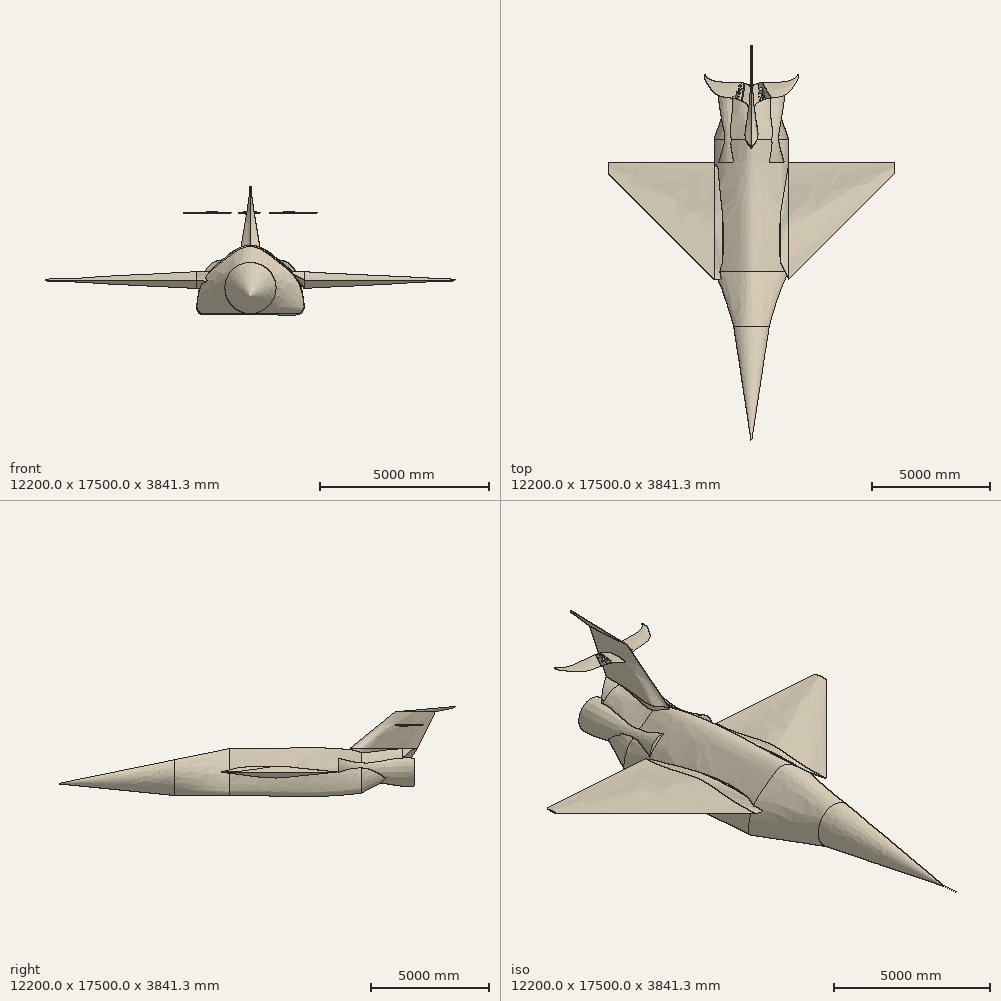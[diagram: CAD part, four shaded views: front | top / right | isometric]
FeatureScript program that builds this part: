
annotation { "Feature Type Name" : "Feature", "Feature Type Description" : "" }
export const myFeature = defineFeature(function(context is Context, id is Id, definition is map)
    precondition{}
    {
        {
            var Q0;
            Q0=qCreatedBy(makeId("Right.planeOp"),FACE);
            var sketch = newSketch(context, id + "F0", { "sketchPlane" : qUnion([Q0])});
            skLineSegment(sketch, "E0", {"start": v(0, 0) * mm, "end": v(-1750, 0) * mm});
            skLineSegment(sketch, "E1", {"start": v(-1750, 0) * mm, "end": v(-3500, 0) * mm});
            skLineSegment(sketch, "E2", {"start": v(-3500, 0) * mm, "end": v(-3500, -1000) * mm});
            skLineSegment(sketch, "E3", {"start": v(-3500, -1000) * mm, "end": v(-8500, -1000) * mm});
            skLineSegment(sketch, "E4", {"start": v(-8500, -1000) * mm, "end": v(-8500, -499.31) * mm});
            skLineSegment(sketch, "E5", {"start": v(-1151.4, 0) * mm, "end": v(-1151.4, 1000) * mm});
            skLineSegment(sketch, "E6", {"start": v(-1151.4, 1000) * mm, "end": v(-8500, -499.31) * mm});
            skLineSegment(sketch, "E7", {"start": v(-8500, -499.31) * mm, "end": v(-3500, -1000) * mm});
            skLineSegment(sketch, "E8", {"start": v(-3500, 0) * mm, "end": v(-3500, 520.82) * mm});
            skLineSegment(sketch, "E9", {"start": v(-8500, -499.31) * mm, "end": v(-8450, -499.31) * mm});
            skLineSegment(sketch, "E10", {"start": v(-8450, -499.31) * mm, "end": v(-8450, -489.1) * mm});
            skLineSegment(sketch, "E11", {"start": v(-8450, -499.31) * mm, "end": v(-8450, -504.32) * mm});
            skSolve(sketch);
        }
        {
            var Q0;
            Q0=sQuery(id+"F0.wireOp",EDGE,"E5");
            cPlane(context, id + "F1", {"entities" : qUnion([Q0]), "cplaneType" : CPlaneType.LINE_ANGLE, "offset" : 25 * mm, "angle" : 90 * degree, "oppositeDirection" : true, "width" : 150 * mm, "height" : 150 * mm});
        }
        {
            var Q0;
            Q0=qCreatedBy(id+"F1.planeOp",FACE);
            var sketch = newSketch(context, id + "F2", { "sketchPlane" : qUnion([Q0])});
            skLineSegment(sketch, "E12.top", {"start": v(-1394.2, -1000) * mm, "end": v(1394.2, -1000) * mm});
            skPoint(sketch, "E12.middle", {"position": v(0, 0) * mm});
            skFitSpline(sketch, "E13", {"points": [v(-1600, -1000) * mm, v(-848, 530) * mm, v(0, 1000) * mm, v(848, 530) * mm, v(1600, -1000) * mm], "startDerivative": vector(0, 10524.75) * mm, "endDerivative": vector(0, -10524.75) * mm});
            skArc(sketch, "E14", {"start": v(-735.27, 618.52) * mm, "mid": v(-1273.27, 435.52) * mm, "end": v(-1440.68, -107.53) * mm});
            skArc(sketch, "E15", {"start": v(1440.68, -107.53) * mm, "mid": v(1273.27, 435.52) * mm, "end": v(735.27, 618.52) * mm});
            skFitSpline(sketch, "E16.trimOffspring", {"points": [v(-1600, -1000) * mm, v(-848, 530) * mm, v(0, 1000) * mm, v(848, 530) * mm, v(1600, -1000) * mm], "startDerivative": vector(0, 10524.75) * mm, "endDerivative": vector(0, -10524.75) * mm});
            skFitSpline(sketch, "E17.trimOffspring", {"points": [v(-1600, -1000) * mm, v(-848, 530) * mm, v(0, 1000) * mm, v(848, 530) * mm, v(1600, -1000) * mm], "startDerivative": vector(0, 10524.75) * mm, "endDerivative": vector(0, -10524.75) * mm});
            skArc(sketch, "E18.filletArc", {"start": v(-1593.82, -787.83) * mm, "mid": v(-1539.85, -937.05) * mm, "end": v(-1394.2, -1000) * mm});
            skArc(sketch, "E19.filletArc", {"start": v(1394.2, -1000) * mm, "mid": v(1539.85, -937.05) * mm, "end": v(1593.82, -787.83) * mm});
            skSolve(sketch);
        }
        {
            var Q0;
            Q0=qCreatedBy(makeId("Front.planeOp"),FACE);
            var sketch = newSketch(context, id + "F3", { "sketchPlane" : qUnion([Q0])});
            skLineSegment(sketch, "E20.top", {"start": v(-1394.2, -1000) * mm, "end": v(1394.2, -1000) * mm});
            skPoint(sketch, "E20.middle", {"position": v(0, 0) * mm});
            skFitSpline(sketch, "E21", {"points": [v(-1600, -1000) * mm, v(-848, 530) * mm, v(0, 1000) * mm, v(848, 530) * mm, v(1600, -1000) * mm], "startDerivative": vector(0, 10524.75) * mm, "endDerivative": vector(0, -10524.75) * mm});
            skArc(sketch, "E22", {"start": v(-735.27, 618.52) * mm, "mid": v(-1273.27, 435.52) * mm, "end": v(-1440.68, -107.53) * mm});
            skArc(sketch, "E23", {"start": v(1440.68, -107.53) * mm, "mid": v(1273.27, 435.52) * mm, "end": v(735.27, 618.52) * mm});
            skFitSpline(sketch, "E24.trimOffspring", {"points": [v(-1600, -1000) * mm, v(-848, 530) * mm, v(0, 1000) * mm, v(848, 530) * mm, v(1600, -1000) * mm], "startDerivative": vector(0, 10524.75) * mm, "endDerivative": vector(0, -10524.75) * mm});
            skFitSpline(sketch, "E25.trimOffspring", {"points": [v(-1600, -1000) * mm, v(-848, 530) * mm, v(0, 1000) * mm, v(848, 530) * mm, v(1600, -1000) * mm], "startDerivative": vector(0, 10524.75) * mm, "endDerivative": vector(0, -10524.75) * mm});
            skArc(sketch, "E26.filletArc", {"start": v(-1593.82, -787.83) * mm, "mid": v(-1539.85, -937.05) * mm, "end": v(-1394.2, -1000) * mm});
            skArc(sketch, "E27.filletArc", {"start": v(1394.2, -1000) * mm, "mid": v(1539.85, -937.05) * mm, "end": v(1593.82, -787.83) * mm});
            skSolve(sketch);
        }
        {
            var Q0;
            Q0=qCreatedBy(makeId("Front.planeOp"),FACE);
            cPlane(context, id + "F4", {"entities" : qUnion([Q0]), "cplaneType" : CPlaneType.OFFSET, "offset" : 3500 * mm, "oppositeDirection" : true, "width" : 150 * mm, "height" : 150 * mm});
        }
        {
            var Q0;
            Q0=qCreatedBy(id+"F4.planeOp",FACE);
            var sketch = newSketch(context, id + "F5", { "sketchPlane" : qUnion([Q0])});
            skLineSegment(sketch, "E28.top", {"start": v(-1394.2, -1000) * mm, "end": v(1394.2, -1000) * mm});
            skPoint(sketch, "E28.middle", {"position": v(0, 0) * mm});
            skFitSpline(sketch, "E29", {"points": [v(-1600, -1000) * mm, v(-848, 530) * mm, v(0, 1000) * mm, v(848, 530) * mm, v(1600, -1000) * mm], "startDerivative": vector(0, 10524.75) * mm, "endDerivative": vector(0, -10524.75) * mm});
            skArc(sketch, "E30", {"start": v(-735.27, 618.52) * mm, "mid": v(-1273.27, 435.52) * mm, "end": v(-1440.68, -107.53) * mm});
            skArc(sketch, "E31", {"start": v(1440.68, -107.53) * mm, "mid": v(1273.27, 435.52) * mm, "end": v(735.27, 618.52) * mm});
            skFitSpline(sketch, "E32.trimOffspring", {"points": [v(-1600, -1000) * mm, v(-848, 530) * mm, v(0, 1000) * mm, v(848, 530) * mm, v(1600, -1000) * mm], "startDerivative": vector(0, 10524.75) * mm, "endDerivative": vector(0, -10524.75) * mm});
            skFitSpline(sketch, "E33.trimOffspring", {"points": [v(-1600, -1000) * mm, v(-848, 530) * mm, v(0, 1000) * mm, v(848, 530) * mm, v(1600, -1000) * mm], "startDerivative": vector(0, 10524.75) * mm, "endDerivative": vector(0, -10524.75) * mm});
            skArc(sketch, "E34.filletArc", {"start": v(-1593.82, -787.83) * mm, "mid": v(-1539.85, -937.05) * mm, "end": v(-1394.2, -1000) * mm});
            skArc(sketch, "E35.filletArc", {"start": v(1394.2, -1000) * mm, "mid": v(1539.85, -937.05) * mm, "end": v(1593.82, -787.83) * mm});
            skSolve(sketch);
        }
        {
            var Q0;
            Q0=qCreatedBy(makeId("Front.planeOp"),FACE);
            cPlane(context, id + "F6", {"entities" : qUnion([Q0]), "cplaneType" : CPlaneType.OFFSET, "offset" : 4500 * mm, "oppositeDirection" : true, "width" : 150 * mm, "height" : 150 * mm});
        }
        {
            var Q0;
            Q0=qCreatedBy(id+"F6.planeOp",FACE);
            var sketch = newSketch(context, id + "F7", { "sketchPlane" : qUnion([Q0])});
            skLineSegment(sketch, "E36.top", {"start": v(-1413.07, -900) * mm, "end": v(1413.07, -900) * mm});
            skPoint(sketch, "E36.middle", {"position": v(0, 0) * mm});
            skFitSpline(sketch, "E37", {"points": [v(-1600, -900) * mm, v(-784.42, 441.24) * mm, v(0, 900) * mm, v(784.42, 441.24) * mm, v(1600, -900) * mm], "startDerivative": vector(0, 9508.62) * mm, "endDerivative": vector(0, -9508.62) * mm});
            skArc(sketch, "E38", {"start": v(-719.25, 488.69) * mm, "mid": v(-1131.76, 394.84) * mm, "end": v(-1324.66, 18.33) * mm});
            skArc(sketch, "E39", {"start": v(1324.66, 18.33) * mm, "mid": v(1131.76, 394.84) * mm, "end": v(719.25, 488.69) * mm});
            skFitSpline(sketch, "E40.trimOffspring", {"points": [v(-1600, -900) * mm, v(-784.42, 441.24) * mm, v(0, 900) * mm, v(784.42, 441.24) * mm, v(1600, -900) * mm], "startDerivative": vector(0, 9508.62) * mm, "endDerivative": vector(0, -9508.62) * mm});
            skFitSpline(sketch, "E41.trimOffspring", {"points": [v(-1600, -900) * mm, v(-784.42, 441.24) * mm, v(0, 900) * mm, v(784.42, 441.24) * mm, v(1600, -900) * mm], "startDerivative": vector(0, 9508.62) * mm, "endDerivative": vector(0, -9508.62) * mm});
            skArc(sketch, "E42.filletArc", {"start": v(-1592.48, -705.43) * mm, "mid": v(-1545.4, -842.02) * mm, "end": v(-1413.07, -900) * mm});
            skArc(sketch, "E43.filletArc", {"start": v(1413.07, -900) * mm, "mid": v(1545.4, -842.02) * mm, "end": v(1592.48, -705.43) * mm});
            skLineSegment(sketch, "E44", {"start": v(-719.25, 488.69) * mm, "end": v(-1324.66, 18.33) * mm, "construction": true});
            skLineSegment(sketch, "E45", {"start": v(719.25, 488.69) * mm, "end": v(1324.66, 18.33) * mm, "construction": true});
            skSolve(sketch);
        }
        {
            var Q0;
            Q0=qCreatedBy(makeId("Front.planeOp"),FACE);
            cPlane(context, id + "F8", {"entities" : qUnion([Q0]), "cplaneType" : CPlaneType.OFFSET, "offset" : 6232.05 * mm, "oppositeDirection" : true, "width" : 150 * mm, "height" : 150 * mm});
        }
        {
            var Q0;
            Q0=qCreatedBy(id+"F8.planeOp",FACE);
            var sketch = newSketch(context, id + "F9", { "sketchPlane" : qUnion([Q0])});
            skArc(sketch, "E46", {"start": v(998.61, 52.63) * mm, "mid": v(0, 1000) * mm, "end": v(-998.61, 52.63) * mm});
            skLineSegment(sketch, "E47", {"start": v(0, 0) * mm, "end": v(-948.68, 0) * mm});
            skLineSegment(sketch, "E48", {"start": v(0, 0) * mm, "end": v(948.68, 0) * mm});
            skLineSegment(sketch, "E49", {"start": v(0, 1000) * mm, "end": v(0, 675) * mm, "construction": true});
            skLineSegment(sketch, "E50", {"start": v(0, 675) * mm, "end": v(-737.82, 675) * mm, "construction": true});
            skLineSegment(sketch, "E51", {"start": v(0, 675) * mm, "end": v(737.82, 675) * mm, "construction": true});
            skPoint(sketch, "E52.visualSharp", {"position": v(-1000, 0) * mm});
            skArc(sketch, "E52.filletArc", {"start": v(-998.61, 52.63) * mm, "mid": v(-984.96, 15.59) * mm, "end": v(-948.68, 0) * mm});
            skPoint(sketch, "E53.visualSharp", {"position": v(1000, 0) * mm});
            skArc(sketch, "E53.filletArc", {"start": v(948.68, 0) * mm, "mid": v(984.96, 15.59) * mm, "end": v(998.61, 52.63) * mm});
            skSolve(sketch);
        }
        {
            var Q0;
            Q0=makeQuery(id+"F2.imprint","IMPRINT",FACE,{"disambiguationData":[TD([[makeQuery(id+"F2.imprint","IMPRINT",EDGE,{"derivedFrom":sQuery(id+"F2.wireOp",EDGE,"E12.top")}),1.0]])]});
            var Q1;
            Q1=makeQuery(id+"F3.imprint","IMPRINT",FACE,{"disambiguationData":[TD([[makeQuery(id+"F3.imprint","IMPRINT",EDGE,{"derivedFrom":sQuery(id+"F3.wireOp",EDGE,"E20.top")}),1.0]])]});
            var Q2;
            Q2=makeQuery(id+"F5.imprint","IMPRINT",FACE,{"disambiguationData":[TD([[makeQuery(id+"F5.imprint","IMPRINT",EDGE,{"derivedFrom":sQuery(id+"F5.wireOp",EDGE,"E28.top")}),1.0]])]});
            var Q3;
            Q3=makeQuery(id+"F7.imprint","IMPRINT",FACE,{"disambiguationData":[TD([[makeQuery(id+"F7.imprint","IMPRINT",EDGE,{"derivedFrom":sQuery(id+"F7.wireOp",EDGE,"E36.top")}),1.0]])]});
            loft(context, id + "F10", {"sheetProfilesArray" : [{ "sheetProfileEntities" : qUnion([Q0]) }, { "sheetProfileEntities" : qUnion([Q1]) }, { "sheetProfileEntities" : qUnion([Q2]) }, { "sheetProfileEntities" : qUnion([Q3]) }]});
        }
        {
            var Q0;
            Q0=sQuery(id+"F7.wireOp",EDGE,"E44");
            var Q1;
            Q1=sQuery(id+"F9.wireOp",VERTEX,"E50.end");
            cPlane(context, id + "F11", {"entities" : qUnion([Q0, Q1]), "cplaneType" : CPlaneType.LINE_ANGLE, "offset" : 25 * mm, "angle" : 180 * degree, "width" : 150 * mm, "height" : 150 * mm});
        }
        {
            var Q0;
            Q0=qCreatedBy(id+"F11.planeOp",FACE);
            var sketch = newSketch(context, id + "F12", { "sketchPlane" : qUnion([Q0])});
            skLineSegment(sketch, "E54", {"start": v(-589.34, 4526.34) * mm, "end": v(-612.8, 6268.32) * mm});
            skLineSegment(sketch, "E55", {"start": v(-1354.08, 4472.19) * mm, "end": v(-612.8, 6268.32) * mm});
            skSolve(sketch);
        }
        {
            var Q0;
            Q0=sQuery(id+"F7.wireOp",EDGE,"E45");
            var Q1;
            Q1=sQuery(id+"F9.wireOp",VERTEX,"E51.end");
            cPlane(context, id + "F13", {"entities" : qUnion([Q0, Q1]), "cplaneType" : CPlaneType.LINE_ANGLE, "offset" : 25 * mm, "angle" : 0 * degree, "width" : 150 * mm, "height" : 150 * mm});
        }
        {
            var Q0;
            Q0=qCreatedBy(id+"F13.planeOp",FACE);
            var sketch = newSketch(context, id + "F14", { "sketchPlane" : qUnion([Q0])});
            skLineSegment(sketch, "E56", {"start": v(589.34, 4526.34) * mm, "end": v(612.8, 6268.32) * mm});
            skLineSegment(sketch, "E57", {"start": v(1354.08, 4472.19) * mm, "end": v(612.8, 6268.32) * mm});
            skSolve(sketch);
        }
        {
            var Q1;
            Q1=makeQuery(id+"F10.opLoft","CAP_FACE",FACE,{"disambiguationData":[OSD([makeQuery(id+"F7.imprint","IMPRINT",FACE,{"disambiguationData":[TD([[makeQuery(id+"F7.imprint","IMPRINT",EDGE,{"derivedFrom":sQuery(id+"F7.wireOp",EDGE,"E36.top")}),1.0]])]})])],"isStart":true});
            var Q2;
            Q2=makeQuery(id+"F9.imprint","IMPRINT",FACE,{"disambiguationData":[TD([[makeQuery(id+"F9.imprint","IMPRINT",EDGE,{"derivedFrom":sQuery(id+"F9.wireOp",EDGE,"E46")}),1.0]])]});
            var Q3;
            Q3=sQuery(id+"F12.wireOp",EDGE,"E54");
            var Q4;
            Q4=sQuery(id+"F14.wireOp",EDGE,"E56");
            loft(context, id + "F15", {"operationType" : NewBodyOperationType.ADD, "addGuides" : true, "sheetProfilesArray" : [{ "sheetProfileEntities" : qUnion([Q1]) }, { "sheetProfileEntities" : qUnion([Q2]) }], "guidesArray" : [{ "guideEntities" : qUnion([Q3]), "guideDerivativeType" : LoftGuideDerivativeType.DEFAULT, "guideDerivativeMagnitude" : 1 }, { "guideEntities" : qUnion([Q4]), "guideDerivativeType" : LoftGuideDerivativeType.DEFAULT, "guideDerivativeMagnitude" : 1 }]});
        }
        {
            var Q0;
            Q0=makeQuery(id+"F15.opLoft","CAP_FACE",FACE,{"disambiguationData":[OSD([makeQuery(id+"F9.imprint","IMPRINT",FACE,{"disambiguationData":[TD([[makeQuery(id+"F9.imprint","IMPRINT",EDGE,{"derivedFrom":sQuery(id+"F9.wireOp",EDGE,"E46")}),1.0]])]})])],"isStart":true});
            extrude(context, id + "F16", {"entities" : qUnion([Q0]), "operationType" : NewBodyOperationType.ADD, "depth" : 649.4 * mm, "offsetDistance" : 25 * mm});
        }
        {
            var Q0;
            Q0=qCreatedBy(makeId("Right.planeOp"),FACE);
            var sketch = newSketch(context, id + "F17", { "sketchPlane" : qUnion([Q0])});
            skLineSegment(sketch, "E58", {"start": v(0, 0) * mm, "end": v(4500, 0) * mm});
            skLineSegment(sketch, "E59", {"start": v(4500, 0) * mm, "end": v(6232.05, 0) * mm});
            skLineSegment(sketch, "E60", {"start": v(4500, 0) * mm, "end": v(4500, 1000) * mm});
            skLineSegment(sketch, "E61", {"start": v(4500, 1000) * mm, "end": v(6881.46, 1000) * mm});
            skLineSegment(sketch, "E62", {"start": v(6881.46, 1000) * mm, "end": v(6881.46, -1000) * mm});
            skLineSegment(sketch, "E63", {"start": v(6881.46, 1000) * mm, "end": v(6232.05, 0) * mm});
            skLineSegment(sketch, "E64", {"start": v(6232.05, 0) * mm, "end": v(5582.64, -1000) * mm});
            skLineSegment(sketch, "E65", {"start": v(5582.64, -1000) * mm, "end": v(6881.46, -1000) * mm});
            skSolve(sketch);
        }
        {
            var Q0;
            Q0=makeQuery(id+"F17.imprint","IMPRINT",FACE,{"disambiguationData":[TD([[makeQuery(id+"F17.imprint","IMPRINT",EDGE,{"derivedFrom":sQuery(id+"F17.wireOp",EDGE,"E62")}),-1.0]])]});
            var Q1;
            Q1=sQuery(id+"F17.wireOp",EDGE,"E61");
            revolve(context, id + "F18", {"operationType" : NewBodyOperationType.REMOVE, "entities" : qUnion([Q0]), "axis" : qUnion([Q1]), "revolveType" : RevolveType.SYMMETRIC, "oppositeDirection" : true, "angle" : 182 * degree});
        }
        {
            var Q0;
            Q0=qCreatedBy(id+"F1.planeOp",FACE);
            var sketch = newSketch(context, id + "F19", { "sketchPlane" : qUnion([Q0])});
            skLineSegment(sketch, "E66.top", {"start": v(-1394.2, -1000) * mm, "end": v(1394.2, -1000) * mm});
            skPoint(sketch, "E66.middle", {"position": v(0, 0) * mm});
            skFitSpline(sketch, "E67", {"points": [v(-1600, -1000) * mm, v(-848, 530) * mm, v(0, 1000) * mm, v(848, 530) * mm, v(1600, -1000) * mm], "startDerivative": vector(0, 10524.75) * mm, "endDerivative": vector(0, -10524.75) * mm});
            skArc(sketch, "E68.filletArc", {"start": v(-1593.82, -787.83) * mm, "mid": v(-1539.85, -937.05) * mm, "end": v(-1394.2, -1000) * mm});
            skArc(sketch, "E69.filletArc", {"start": v(1394.2, -1000) * mm, "mid": v(1539.85, -937.05) * mm, "end": v(1593.82, -787.83) * mm});
            skLineSegment(sketch, "E70", {"start": v(-1593.82, -787.83) * mm, "end": v(-1394.2, -1000) * mm, "construction": true});
            skLineSegment(sketch, "E71", {"start": v(1593.82, -787.83) * mm, "end": v(1394.2, -1000) * mm, "construction": true});
            skSolve(sketch);
        }
        {
            var Q0;
            Q0=qCreatedBy(makeId("Front.planeOp"),FACE);
            cPlane(context, id + "F20", {"entities" : qUnion([Q0]), "cplaneType" : CPlaneType.OFFSET, "offset" : 3500 * mm, "width" : 150 * mm, "height" : 150 * mm});
        }
        {
            var Q0;
            Q0=qCreatedBy(id+"F20.planeOp",FACE);
            var sketch = newSketch(context, id + "F21", { "sketchPlane" : qUnion([Q0])});
            skCircle(sketch, "E72", {"center": v(0, -239.59) * mm, "radius": 760.41 * mm});
            skLineSegment(sketch, "E73", {"start": v(0, -1000) * mm, "end": v(0, -800) * mm, "construction": true});
            skLineSegment(sketch, "E74", {"start": v(0, -800) * mm, "end": v(-513.97, -800) * mm, "construction": true});
            skLineSegment(sketch, "E75", {"start": v(0, -800) * mm, "end": v(513.97, -800) * mm, "construction": true});
            skSolve(sketch);
        }
        {
            var Q0;
            Q0=qCreatedBy(makeId("Front.planeOp"),FACE);
            cPlane(context, id + "F22", {"entities" : qUnion([Q0]), "cplaneType" : CPlaneType.OFFSET, "offset" : 8450 * mm, "width" : 150 * mm, "height" : 150 * mm});
        }
        {
            var Q0;
            Q0=qCreatedBy(id+"F22.planeOp",FACE);
            var sketch = newSketch(context, id + "F23", { "sketchPlane" : qUnion([Q0])});
            skCircle(sketch, "E76", {"center": v(0, -496.71) * mm, "radius": 7.6 * mm});
            skSolve(sketch);
        }
        {
            var Q0;
            Q0=sQuery(id+"F19.wireOp",EDGE,"E70");
            var Q1;
            Q1=sQuery(id+"F21.wireOp",VERTEX,"E74.end");
            cPlane(context, id + "F24", {"entities" : qUnion([Q0, Q1]), "cplaneType" : CPlaneType.LINE_ANGLE, "offset" : 25 * mm, "angle" : 0 * degree, "width" : 150 * mm, "height" : 150 * mm});
        }
        {
            var Q0;
            Q0=qCreatedBy(id+"F24.planeOp",FACE);
            var sketch = newSketch(context, id + "F25", { "sketchPlane" : qUnion([Q0])});
            skLineSegment(sketch, "E77", {"start": v(3032.27, -230.44) * mm, "end": v(558.11, 518.4) * mm});
            skLineSegment(sketch, "E78", {"start": v(3032.27, -230.44) * mm, "end": v(558.11, 227.09) * mm});
            skSolve(sketch);
        }
        {
            var Q0;
            Q0=sQuery(id+"F19.wireOp",EDGE,"E71");
            var Q1;
            Q1=sQuery(id+"F21.wireOp",VERTEX,"E75.end");
            cPlane(context, id + "F26", {"entities" : qUnion([Q0, Q1]), "cplaneType" : CPlaneType.LINE_ANGLE, "offset" : 25 * mm, "angle" : 180 * degree, "width" : 150 * mm, "height" : 150 * mm});
        }
        {
            var Q0;
            Q0=qCreatedBy(id+"F26.planeOp",FACE);
            var sketch = newSketch(context, id + "F27", { "sketchPlane" : qUnion([Q0])});
            skLineSegment(sketch, "E79", {"start": v(-3032.27, -230.44) * mm, "end": v(-558.11, 518.4) * mm});
            skLineSegment(sketch, "E80", {"start": v(-3032.27, -230.44) * mm, "end": v(-558.11, 227.09) * mm});
            skSolve(sketch);
        }
        {
            var Q1;
            Q1=makeQuery(id+"F19.imprint","IMPRINT",FACE,{"disambiguationData":[TD([[makeQuery(id+"F19.imprint","IMPRINT",EDGE,{"derivedFrom":sQuery(id+"F19.wireOp",EDGE,"E66.top")}),1.0]])]});
            var Q2;
            Q2=makeQuery(id+"F21.imprint","IMPRINT",FACE,{"disambiguationData":[TD([[makeQuery(id+"F21.imprint","IMPRINT",EDGE,{"derivedFrom":sQuery(id+"F21.wireOp",EDGE,"E72")}),1.0]])]});
            var Q3;
            Q3=sQuery(id+"F25.wireOp",EDGE,"E77");
            var Q4;
            Q4=sQuery(id+"F27.wireOp",EDGE,"E79");
            loft(context, id + "F28", {"operationType" : NewBodyOperationType.ADD, "addGuides" : true, "sheetProfilesArray" : [{ "sheetProfileEntities" : qUnion([Q1]) }, { "sheetProfileEntities" : qUnion([Q2]) }], "guidesArray" : [{ "guideEntities" : qUnion([Q3]), "guideDerivativeType" : LoftGuideDerivativeType.DEFAULT, "guideDerivativeMagnitude" : 1 }, { "guideEntities" : qUnion([Q4]), "guideDerivativeType" : LoftGuideDerivativeType.DEFAULT, "guideDerivativeMagnitude" : 1 }]});
        }
        {
            var Q1;
            Q1=makeQuery(id+"F28.opLoft","CAP_FACE",FACE,{"disambiguationData":[OSD([makeQuery(id+"F21.imprint","IMPRINT",FACE,{"disambiguationData":[TD([[makeQuery(id+"F21.imprint","IMPRINT",EDGE,{"derivedFrom":sQuery(id+"F21.wireOp",EDGE,"E72")}),1.0]])]})])],"isStart":true});
            var Q2;
            Q2=makeQuery(id+"F23.imprint","IMPRINT",FACE,{"disambiguationData":[TD([[makeQuery(id+"F23.imprint","IMPRINT",EDGE,{"derivedFrom":sQuery(id+"F23.wireOp",EDGE,"E76")}),1.0]])]});
            loft(context, id + "F29", {"operationType" : NewBodyOperationType.ADD, "sheetProfilesArray" : [{ "sheetProfileEntities" : qUnion([Q1]) }, { "sheetProfileEntities" : qUnion([Q2]) }]});
        }
        {
            var Q0;
            Q0=makeQuery(id+"F29.opLoft","CAP_FACE",FACE,{"disambiguationData":[OSD([makeQuery(id+"F23.imprint","IMPRINT",FACE,{"disambiguationData":[TD([[makeQuery(id+"F23.imprint","IMPRINT",EDGE,{"derivedFrom":sQuery(id+"F23.wireOp",EDGE,"E76")}),1.0]])]})])],"isStart":true});
            extrude(context, id + "F30", {"entities" : qUnion([Q0]), "operationType" : NewBodyOperationType.ADD, "depth" : 550 * mm, "offsetDistance" : 25 * mm});
        }
        {
            var Q0;
            Q0=qCreatedBy(makeId("Front.planeOp"),FACE);
            cPlane(context, id + "F31", {"entities" : qUnion([Q0]), "cplaneType" : CPlaneType.OFFSET, "offset" : 3500 * mm, "oppositeDirection" : true, "width" : 150 * mm, "height" : 150 * mm});
        }
        {
            var Q0;
            Q0=qCreatedBy(id+"F31.planeOp",FACE);
            var sketch = newSketch(context, id + "F32", { "sketchPlane" : qUnion([Q0])});
            skCircle(sketch, "E81", {"center": v(-800, 0) * mm, "radius": 600 * mm});
            skCircle(sketch, "E82", {"center": v(800, 0) * mm, "radius": 600 * mm});
            skSolve(sketch);
        }
        {
            var Q0;
            Q0=qCreatedBy(makeId("Front.planeOp"),FACE);
            cPlane(context, id + "F33", {"entities" : qUnion([Q0]), "cplaneType" : CPlaneType.OFFSET, "offset" : 4500 * mm, "oppositeDirection" : true, "width" : 150 * mm, "height" : 150 * mm});
        }
        {
            var Q0;
            Q0=qCreatedBy(id+"F33.planeOp",FACE);
            var sketch = newSketch(context, id + "F34", { "sketchPlane" : qUnion([Q0])});
            skCircle(sketch, "E83", {"center": v(-800, 0) * mm, "radius": 400 * mm});
            skCircle(sketch, "E84", {"center": v(800, 0) * mm, "radius": 400 * mm});
            skSolve(sketch);
        }
        {
            var Q0;
            Q0=qCreatedBy(makeId("Front.planeOp"),FACE);
            cPlane(context, id + "F35", {"entities" : qUnion([Q0]), "cplaneType" : CPlaneType.OFFSET, "offset" : 6232.05 * mm, "oppositeDirection" : true, "width" : 150 * mm, "height" : 150 * mm});
        }
        {
            var Q0;
            Q0=qCreatedBy(id+"F35.planeOp",FACE);
            var sketch = newSketch(context, id + "F36", { "sketchPlane" : qUnion([Q0])});
            skCircle(sketch, "E85", {"center": v(-800, 0) * mm, "radius": 600 * mm});
            skCircle(sketch, "E86", {"center": v(800, 0) * mm, "radius": 600 * mm});
            skSolve(sketch);
        }
        {
            var Q0;
            Q0=qCreatedBy(makeId("Front.planeOp"),FACE);
            cPlane(context, id + "F37", {"entities" : qUnion([Q0]), "cplaneType" : CPlaneType.OFFSET, "offset" : 6732.05 * mm, "oppositeDirection" : true, "width" : 150 * mm, "height" : 150 * mm});
        }
        {
            var Q0;
            Q0=qCreatedBy(id+"F37.planeOp",FACE);
            var sketch = newSketch(context, id + "F38", { "sketchPlane" : qUnion([Q0])});
            skCircle(sketch, "E87", {"center": v(-800, 0) * mm, "radius": 600 * mm});
            skCircle(sketch, "E88", {"center": v(800, 0) * mm, "radius": 600 * mm});
            skSolve(sketch);
        }
        {
            var Q0;
            Q0=makeQuery(id+"F32.imprint","IMPRINT",FACE,{"disambiguationData":[TD([[makeQuery(id+"F32.imprint","IMPRINT",EDGE,{"derivedFrom":sQuery(id+"F32.wireOp",EDGE,"E81")}),1.0]])]});
            var Q1;
            Q1=makeQuery(id+"F34.imprint","IMPRINT",FACE,{"disambiguationData":[TD([[makeQuery(id+"F34.imprint","IMPRINT",EDGE,{"derivedFrom":sQuery(id+"F34.wireOp",EDGE,"E83")}),1.0]])]});
            var Q2;
            Q2=makeQuery(id+"F36.imprint","IMPRINT",FACE,{"disambiguationData":[TD([[makeQuery(id+"F36.imprint","IMPRINT",EDGE,{"derivedFrom":sQuery(id+"F36.wireOp",EDGE,"E85")}),1.0]])]});
            var Q3;
            Q3=makeQuery(id+"F38.imprint","IMPRINT",FACE,{"disambiguationData":[TD([[makeQuery(id+"F38.imprint","IMPRINT",EDGE,{"derivedFrom":sQuery(id+"F38.wireOp",EDGE,"E87")}),1.0]])]});
            loft(context, id + "F39", {"sheetProfilesArray" : [{ "sheetProfileEntities" : qUnion([Q0]) }, { "sheetProfileEntities" : qUnion([Q1]) }, { "sheetProfileEntities" : qUnion([Q2]) }, { "sheetProfileEntities" : qUnion([Q3]) }]});
        }
        {
            var Q0;
            Q0=makeQuery(id+"F32.imprint","IMPRINT",FACE,{"disambiguationData":[TD([[makeQuery(id+"F32.imprint","IMPRINT",EDGE,{"derivedFrom":sQuery(id+"F32.wireOp",EDGE,"E82")}),1.0]])]});
            var Q1;
            Q1=makeQuery(id+"F34.imprint","IMPRINT",FACE,{"disambiguationData":[TD([[makeQuery(id+"F34.imprint","IMPRINT",EDGE,{"derivedFrom":sQuery(id+"F34.wireOp",EDGE,"E84")}),1.0]])]});
            var Q2;
            Q2=makeQuery(id+"F36.imprint","IMPRINT",FACE,{"disambiguationData":[TD([[makeQuery(id+"F36.imprint","IMPRINT",EDGE,{"derivedFrom":sQuery(id+"F36.wireOp",EDGE,"E86")}),1.0]])]});
            var Q3;
            Q3=makeQuery(id+"F38.imprint","IMPRINT",FACE,{"disambiguationData":[TD([[makeQuery(id+"F38.imprint","IMPRINT",EDGE,{"derivedFrom":sQuery(id+"F38.wireOp",EDGE,"E88")}),1.0]])]});
            loft(context, id + "F40", {"sheetProfilesArray" : [{ "sheetProfileEntities" : qUnion([Q0]) }, { "sheetProfileEntities" : qUnion([Q1]) }, { "sheetProfileEntities" : qUnion([Q2]) }, { "sheetProfileEntities" : qUnion([Q3]) }]});
        }
        {
            var Q0;
            Q0=qCreatedBy(makeId("Right.planeOp"),FACE);
            var sketch = newSketch(context, id + "F41", { "sketchPlane" : qUnion([Q0])});
            skFitSpline(sketch, "E89", {"points": [v(-1500, -50) * mm, v(0, 250) * mm, v(3000, -50) * mm, v(0, -250) * mm, v(-1500, -50) * mm]});
            skSolve(sketch);
        }
        {
            var Q0;
            Q0=qCreatedBy(makeId("Right.planeOp"),FACE);
            cPlane(context, id + "F42", {"entities" : qUnion([Q0]), "cplaneType" : CPlaneType.OFFSET, "offset" : 1600 * mm, "oppositeDirection" : true, "width" : 150 * mm, "height" : 150 * mm});
        }
        {
            var Q0;
            Q0=qCreatedBy(id+"F42.planeOp",FACE);
            var sketch = newSketch(context, id + "F43", { "sketchPlane" : qUnion([Q0])});
            skFitSpline(sketch, "E90", {"points": [v(-1500, 0) * mm, v(1000, 250) * mm, v(3500, 0) * mm], "startDerivative": vector(7500, 0) * mm, "endDerivative": vector(7500, 0) * mm});
            skFitSpline(sketch, "E91", {"points": [v(-1500, 0) * mm, v(1000, -250) * mm, v(3500, 0) * mm], "startDerivative": vector(5000, -750) * mm, "endDerivative": vector(7500, 0) * mm});
            skSolve(sketch);
        }
        {
            var Q0;
            Q0=qCreatedBy(makeId("Right.planeOp"),FACE);
            cPlane(context, id + "F44", {"entities" : qUnion([Q0]), "cplaneType" : CPlaneType.OFFSET, "offset" : 1600 * mm, "width" : 150 * mm, "height" : 150 * mm});
        }
        {
            var Q0;
            Q0=qCreatedBy(id+"F44.planeOp",FACE);
            var sketch = newSketch(context, id + "F45", { "sketchPlane" : qUnion([Q0])});
            skFitSpline(sketch, "E92", {"points": [v(-1500, 0) * mm, v(1000, 250) * mm, v(3500, 0) * mm], "startDerivative": vector(7500, 0) * mm, "endDerivative": vector(7500, 0) * mm});
            skFitSpline(sketch, "E93", {"points": [v(-1500, 0) * mm, v(1000, -250) * mm, v(3500, 0) * mm], "startDerivative": vector(5000, -750) * mm, "endDerivative": vector(7500, 0) * mm});
            skSolve(sketch);
        }
        {
            var Q0;
            Q0=qCreatedBy(makeId("Right.planeOp"),FACE);
            cPlane(context, id + "F46", {"entities" : qUnion([Q0]), "cplaneType" : CPlaneType.OFFSET, "offset" : 6100 * mm, "oppositeDirection" : true, "width" : 150 * mm, "height" : 150 * mm});
        }
        {
            var Q0;
            Q0=qCreatedBy(id+"F46.planeOp",FACE);
            var sketch = newSketch(context, id + "F47", { "sketchPlane" : qUnion([Q0])});
            skFitSpline(sketch, "E94", {"points": [v(3000, 0) * mm, v(3250, 25) * mm, v(3500, 0) * mm], "startDerivative": vector(750, 0) * mm, "endDerivative": vector(750, 0) * mm});
            skFitSpline(sketch, "E95", {"points": [v(3000, 0) * mm, v(3250, -25) * mm, v(3500, 0) * mm], "startDerivative": vector(500, -75) * mm, "endDerivative": vector(750, 0) * mm});
            skSolve(sketch);
        }
        {
            var Q0;
            Q0=qCreatedBy(makeId("Right.planeOp"),FACE);
            cPlane(context, id + "F48", {"entities" : qUnion([Q0]), "cplaneType" : CPlaneType.OFFSET, "offset" : 6100 * mm, "width" : 150 * mm, "height" : 150 * mm});
        }
        {
            var Q0;
            Q0=qCreatedBy(id+"F48.planeOp",FACE);
            var sketch = newSketch(context, id + "F49", { "sketchPlane" : qUnion([Q0])});
            skFitSpline(sketch, "E96", {"points": [v(3000, 0) * mm, v(3250, 25) * mm, v(3500, 0) * mm], "startDerivative": vector(750, 0) * mm, "endDerivative": vector(750, 0) * mm});
            skFitSpline(sketch, "E97", {"points": [v(3000, 0) * mm, v(3250, -25) * mm, v(3500, 0) * mm], "startDerivative": vector(500, -75) * mm, "endDerivative": vector(750, 0) * mm});
            skSolve(sketch);
        }
        {
            var Q0;
            Q0=qSketchRegion(id+"F41",true);
            extrude(context, id + "F50", {"entities" : qUnion([Q0]), "endBound" : BoundingType.SYMMETRIC, "depth" : 2500 * mm, "offsetDistance" : 25 * mm});
        }
        {
            var Q1;
            Q1=makeQuery(id+"F50.opExtrude","CAP_FACE",FACE,{"disambiguationData":[OSD([sQuery(id+"F41.wireOp",EDGE,"E89")])],"isStart":true});
            var Q2;
            {var subQ0=sQuery(id+"F43.wireOp",EDGE,"E90");Q2=makeQuery(id+"F43.imprint","IMPRINT",FACE,{"disambiguationData":[TD([[makeQuery(id+"F43.imprint","IMPRINT",EDGE,{"derivedFrom":subQ0}),-1.0]])]});}
            loft(context, id + "F51", {"operationType" : NewBodyOperationType.ADD, "sheetProfilesArray" : [{ "sheetProfileEntities" : qUnion([Q1]) }, { "sheetProfileEntities" : qUnion([Q2]) }]});
        }
        {
            var Q1;
            Q1=makeQuery(id+"F50.opExtrude","CAP_FACE",FACE,{"disambiguationData":[OSD([sQuery(id+"F41.wireOp",EDGE,"E89")])],"isStart":false});
            var Q2;
            {var subQ0=sQuery(id+"F45.wireOp",EDGE,"E92");Q2=makeQuery(id+"F45.imprint","IMPRINT",FACE,{"disambiguationData":[TD([[makeQuery(id+"F45.imprint","IMPRINT",EDGE,{"derivedFrom":subQ0}),-1.0]])]});}
            loft(context, id + "F52", {"operationType" : NewBodyOperationType.ADD, "sheetProfilesArray" : [{ "sheetProfileEntities" : qUnion([Q1]) }, { "sheetProfileEntities" : qUnion([Q2]) }]});
        }
        {
            var Q1;
            {var subQ0=sQuery(id+"F43.wireOp",EDGE,"E90");Q1=makeQuery(id+"F51.opLoft","CAP_FACE",FACE,{"disambiguationData":[OSD([makeQuery(id+"F43.imprint","IMPRINT",FACE,{"disambiguationData":[TD([[makeQuery(id+"F43.imprint","IMPRINT",EDGE,{"derivedFrom":subQ0}),-1.0]])]})])],"isStart":true});}
            var Q2;
            {var subQ0=sQuery(id+"F47.wireOp",EDGE,"E94");Q2=makeQuery(id+"F47.imprint","IMPRINT",FACE,{"disambiguationData":[TD([[makeQuery(id+"F47.imprint","IMPRINT",EDGE,{"derivedFrom":subQ0}),-1.0]])]});}
            loft(context, id + "F53", {"operationType" : NewBodyOperationType.ADD, "sheetProfilesArray" : [{ "sheetProfileEntities" : qUnion([Q1]) }, { "sheetProfileEntities" : qUnion([Q2]) }]});
        }
        {
            var Q1;
            {var subQ0=sQuery(id+"F45.wireOp",EDGE,"E92");Q1=makeQuery(id+"F52.opLoft","CAP_FACE",FACE,{"disambiguationData":[OSD([makeQuery(id+"F45.imprint","IMPRINT",FACE,{"disambiguationData":[TD([[makeQuery(id+"F45.imprint","IMPRINT",EDGE,{"derivedFrom":subQ0}),-1.0]])]})])],"isStart":true});}
            var Q2;
            {var subQ0=sQuery(id+"F49.wireOp",EDGE,"E96");Q2=makeQuery(id+"F49.imprint","IMPRINT",FACE,{"disambiguationData":[TD([[makeQuery(id+"F49.imprint","IMPRINT",EDGE,{"derivedFrom":subQ0}),-1.0]])]});}
            loft(context, id + "F54", {"operationType" : NewBodyOperationType.ADD, "sheetProfilesArray" : [{ "sheetProfileEntities" : qUnion([Q1]) }, { "sheetProfileEntities" : qUnion([Q2]) }]});
        }
        {
            var Q0;
            Q0=qCreatedBy(makeId("Right.planeOp"),FACE);
            var sketch = newSketch(context, id + "F55", { "sketchPlane" : qUnion([Q0])});
            skLineSegment(sketch, "E98", {"start": v(0, 0) * mm, "end": v(4500, 0) * mm});
            skLineSegment(sketch, "E99", {"start": v(4500, 0) * mm, "end": v(4500, 1000) * mm});
            skLineSegment(sketch, "E100", {"start": v(4500, 1000) * mm, "end": v(4500, 750) * mm});
            skLineSegment(sketch, "E101", {"start": v(4500, 750) * mm, "end": v(4000, 750) * mm});
            skLineSegment(sketch, "E102", {"start": v(4500, 750) * mm, "end": v(6250, 750) * mm});
            skLineSegment(sketch, "E103", {"start": v(4500, 1000) * mm, "end": v(4000, 1000) * mm});
            skLineSegment(sketch, "E104", {"start": v(4500, 1000) * mm, "end": v(6881.46, 1000) * mm});
            skLineSegment(sketch, "E105", {"start": v(6881.46, 1000) * mm, "end": v(8500, 1000) * mm});
            skLineSegment(sketch, "E106", {"start": v(8500, 1000) * mm, "end": v(8500, 2800) * mm});
            skLineSegment(sketch, "E107", {"start": v(6881.46, 1000) * mm, "end": v(7648.6, 2572.89) * mm});
            skLineSegment(sketch, "E108", {"start": v(7648.6, 2572.89) * mm, "end": v(5943.2, 2572.89) * mm});
            skLineSegment(sketch, "E109", {"start": v(5943.2, 2572.89) * mm, "end": v(4000, 1000) * mm});
            skSolve(sketch);
        }
        {
            var Q0;
            Q0=qCreatedBy(makeId("Top.planeOp"),FACE);
            cPlane(context, id + "F56", {"entities" : qUnion([Q0]), "cplaneType" : CPlaneType.OFFSET, "offset" : 750 * mm, "width" : 150 * mm, "height" : 150 * mm});
        }
        {
            var Q0;
            Q0=qCreatedBy(id+"F56.planeOp",FACE);
            var sketch = newSketch(context, id + "F57", { "sketchPlane" : qUnion([Q0])});
            skFitSpline(sketch, "E110", {"points": [v(0, 4000) * mm, v(-250, 4500) * mm, v(0, 6250) * mm], "startDerivative": vector(-889.86, 1147.1) * mm, "endDerivative": vector(737.87, 3164.53) * mm});
            skFitSpline(sketch, "E111", {"points": [v(0, 4000) * mm, v(250, 4500) * mm, v(0, 6250) * mm], "startDerivative": vector(889.86, 1147.1) * mm, "endDerivative": vector(-737.87, 3164.53) * mm});
            skSolve(sketch);
        }
        {
            var Q0;
            Q0=qCreatedBy(makeId("Top.planeOp"),FACE);
            cPlane(context, id + "F58", {"entities" : qUnion([Q0]), "cplaneType" : CPlaneType.OFFSET, "offset" : 1000 * mm, "width" : 150 * mm, "height" : 150 * mm});
        }
        {
            var Q0;
            Q0=qCreatedBy(id+"F58.planeOp",FACE);
            var sketch = newSketch(context, id + "F59", { "sketchPlane" : qUnion([Q0])});
            skFitSpline(sketch, "E112", {"points": [v(0, 4000) * mm, v(-250, 4500) * mm, v(0, 6881.46) * mm], "startDerivative": vector(0, 2302.24) * mm, "endDerivative": vector(0, 5298.17) * mm});
            skFitSpline(sketch, "E113", {"points": [v(0, 4000) * mm, v(250, 4500) * mm, v(0, 6881.46) * mm], "startDerivative": vector(0, 2302.24) * mm, "endDerivative": vector(0, 5298.17) * mm});
            skSolve(sketch);
        }
        {
            var Q0;
            Q0=sQuery(id+"F55.wireOp",EDGE,"E108");
            cPlane(context, id + "F60", {"entities" : qUnion([Q0]), "cplaneType" : CPlaneType.LINE_ANGLE, "offset" : 25 * mm, "angle" : 180 * degree, "width" : 150 * mm, "height" : 150 * mm});
        }
        {
            var Q0;
            Q0=qCreatedBy(id+"F60.planeOp",FACE);
            var sketch = newSketch(context, id + "F61", { "sketchPlane" : qUnion([Q0])});
            skFitSpline(sketch, "E114", {"points": [v(0, 5943.2) * mm, v(-25, 6795.9) * mm, v(0, 7648.6) * mm], "startDerivative": vector(-75, 1705.4) * mm, "endDerivative": vector(75, 1705.4) * mm});
            skFitSpline(sketch, "E115", {"points": [v(0, 5943.2) * mm, v(25, 6795.9) * mm, v(0, 7648.6) * mm], "startDerivative": vector(75, 1705.4) * mm, "endDerivative": vector(-75, 1705.4) * mm});
            skSolve(sketch);
        }
        {
            var Q0;
            Q0=qCreatedBy(makeId("Front.planeOp"),FACE);
            cPlane(context, id + "F62", {"entities" : qUnion([Q0]), "cplaneType" : CPlaneType.OFFSET, "offset" : 8500 * mm, "oppositeDirection" : true, "width" : 150 * mm, "height" : 150 * mm});
        }
        {
            var Q0;
            Q0=qCreatedBy(id+"F62.planeOp",FACE);
            var sketch = newSketch(context, id + "F63", { "sketchPlane" : qUnion([Q0])});
            skCircle(sketch, "E116", {"center": v(0, 2775) * mm, "radius": 25 * mm});
            skSolve(sketch);
        }
        {
            var Q0;
            Q0=qCreatedBy(makeId("Right.planeOp"),FACE);
            var sketch = newSketch(context, id + "F64", { "sketchPlane" : qUnion([Q0])});
            skLineSegment(sketch, "E117", {"start": v(5943.2, 2572.89) * mm, "end": v(8500, 2800) * mm});
            skSolve(sketch);
        }
        {
            var Q1;
            Q1=qSketchRegion(id+"F57",true);
            var Q2;
            Q2=qSketchRegion(id+"F59",true);
            loft(context, id + "F65", {"sheetProfilesArray" : [{ "sheetProfileEntities" : qUnion([Q1]) }, { "sheetProfileEntities" : qUnion([Q2]) }]});
        }
        {
            var Q1;
            {var subQ0=sQuery(id+"F59.wireOp",EDGE,"E112");Q1=makeQuery(id+"F65.opLoft","CAP_FACE",FACE,{"disambiguationData":[OSD([makeQuery(id+"F59.imprint","IMPRINT",FACE,{"disambiguationData":[TD([[makeQuery(id+"F59.imprint","IMPRINT",EDGE,{"derivedFrom":subQ0}),-1.0]])]})])],"isStart":true});}
            var Q2;
            Q2=makeQuery(id+"F61.imprint","IMPRINT",FACE,{"disambiguationData":[TD([[makeQuery(id+"F61.imprint","IMPRINT",EDGE,{"derivedFrom":sQuery(id+"F61.wireOp",EDGE,"E114")}),-1.0]])]});
            loft(context, id + "F66", {"operationType" : NewBodyOperationType.ADD, "sheetProfilesArray" : [{ "sheetProfileEntities" : qUnion([Q1]) }, { "sheetProfileEntities" : qUnion([Q2]) }]});
        }
        {
            var Q1;
            Q1=makeQuery(id+"F66.opLoft","CAP_FACE",FACE,{"disambiguationData":[OSD([makeQuery(id+"F61.imprint","IMPRINT",FACE,{"disambiguationData":[TD([[makeQuery(id+"F61.imprint","IMPRINT",EDGE,{"derivedFrom":sQuery(id+"F61.wireOp",EDGE,"E114")}),-1.0]])]})])],"isStart":true});
            var Q2;
            Q2=makeQuery(id+"F63.imprint","IMPRINT",FACE,{"disambiguationData":[TD([[makeQuery(id+"F63.imprint","IMPRINT",EDGE,{"derivedFrom":sQuery(id+"F63.wireOp",EDGE,"E116")}),1.0]])]});
            var Q3;
            Q3=sQuery(id+"F64.wireOp",EDGE,"E117");
            loft(context, id + "F67", {"operationType" : NewBodyOperationType.ADD, "addGuides" : true, "sheetProfilesArray" : [{ "sheetProfileEntities" : qUnion([Q1]) }, { "sheetProfileEntities" : qUnion([Q2]) }], "guidesArray" : [{ "guideEntities" : qUnion([Q3]), "guideDerivativeType" : LoftGuideDerivativeType.DEFAULT, "guideDerivativeMagnitude" : 1 }]});
        }
        {
            var Q0;
            Q0=qCreatedBy(makeId("Top.planeOp"),FACE);
            cPlane(context, id + "F68", {"entities" : qUnion([Q0]), "cplaneType" : CPlaneType.OFFSET, "offset" : 2000 * mm, "width" : 150 * mm, "height" : 150 * mm});
        }
        {
            var Q0;
            Q0=qCreatedBy(id+"F68.planeOp",FACE);
            var sketch = newSketch(context, id + "F69", { "sketchPlane" : qUnion([Q0])});
            skLineSegment(sketch, "E118", {"start": v(0, 0) * mm, "end": v(0, 4500) * mm});
            skLineSegment(sketch, "E119", {"start": v(0, 4500) * mm, "end": v(0, 7369.2) * mm});
            skLineSegment(sketch, "E120", {"start": v(0, 7369.2) * mm, "end": v(0, 5235.43) * mm});
            skLineSegment(sketch, "E121", {"start": v(0, 6302.31) * mm, "end": v(0, 5302.31) * mm});
            skLineSegment(sketch, "E122", {"start": v(0, 6302.31) * mm, "end": v(0, 7302.31) * mm});
            skLineSegment(sketch, "E123", {"start": v(0, 6302.31) * mm, "end": v(0, 6552.31) * mm});
            skLineSegment(sketch, "E124", {"start": v(0, 6302.31) * mm, "end": v(-1200, 6302.31) * mm});
            skLineSegment(sketch, "E125", {"start": v(0, 6302.31) * mm, "end": v(1200, 6302.31) * mm});
            skLineSegment(sketch, "E126", {"start": v(0, 6552.31) * mm, "end": v(-1700, 6552.31) * mm});
            skLineSegment(sketch, "E127", {"start": v(0, 6552.31) * mm, "end": v(1700, 6552.31) * mm});
            skLineSegment(sketch, "E128", {"start": v(0, 7302.31) * mm, "end": v(-2000, 7302.31) * mm});
            skLineSegment(sketch, "E129", {"start": v(0, 7302.31) * mm, "end": v(2000, 7302.31) * mm});
            skLineSegment(sketch, "E130", {"start": v(-2000, 7302.31) * mm, "end": v(-2000, 7052.31) * mm});
            skLineSegment(sketch, "E131", {"start": v(2000, 7302.31) * mm, "end": v(2000, 7052.31) * mm});
            skFitSpline(sketch, "E132", {"points": [v(0, 5302.31) * mm, v(-1200, 6302.31) * mm, v(-2000, 7052.31) * mm], "startDerivative": vector(0, 5513.6) * mm, "endDerivative": vector(-1974.16, 3290.27) * mm});
            skFitSpline(sketch, "E133", {"points": [v(0, 5302.31) * mm, v(1200, 6302.31) * mm, v(2000, 7052.31) * mm], "startDerivative": vector(0, 5513.6) * mm, "endDerivative": vector(1974.16, 3290.27) * mm});
            skFitSpline(sketch, "E134", {"points": [v(0, 6552.31) * mm, v(-2000, 7302.31) * mm], "startDerivative": vector(0, 2250) * mm, "endDerivative": vector(-900, 2250) * mm});
            skFitSpline(sketch, "E135", {"points": [v(0, 6552.31) * mm, v(2000, 7302.31) * mm], "startDerivative": vector(0, 2250) * mm, "endDerivative": vector(900, 2250) * mm});
            skSolve(sketch);
        }
        {
            var Q0;
            Q0=qCreatedBy(makeId("Right.planeOp"),FACE);
            var sketch = newSketch(context, id + "F70", { "sketchPlane" : qUnion([Q0])});
            skFitSpline(sketch, "E136", {"points": [v(5302.31, 2000) * mm, v(5927.31, 2050) * mm, v(6552.31, 2000) * mm], "startDerivative": vector(1250, 150) * mm, "endDerivative": vector(1250, -150) * mm});
            skFitSpline(sketch, "E137", {"points": [v(5302.31, 2000) * mm, v(5927.31, 1950) * mm, v(6552.31, 2000) * mm], "startDerivative": vector(1250, -150) * mm, "endDerivative": vector(1250, 150) * mm});
            skSolve(sketch);
        }
        {
            var Q0;
            Q0=qCreatedBy(makeId("Right.planeOp"),FACE);
            cPlane(context, id + "F71", {"entities" : qUnion([Q0]), "cplaneType" : CPlaneType.OFFSET, "offset" : 2000 * mm, "oppositeDirection" : true, "width" : 150 * mm, "height" : 150 * mm});
        }
        {
            var Q0;
            Q0=qCreatedBy(id+"F71.planeOp",FACE);
            var sketch = newSketch(context, id + "F72", { "sketchPlane" : qUnion([Q0])});
            skFitSpline(sketch, "E138", {"points": [v(7052.31, 2000) * mm, v(7177.31, 2010) * mm, v(7302.31, 2000) * mm], "startDerivative": vector(250, 30) * mm, "endDerivative": vector(250, -30) * mm});
            skFitSpline(sketch, "E139", {"points": [v(7052.31, 2000) * mm, v(7177.31, 1990) * mm, v(7302.31, 2000) * mm], "startDerivative": vector(250, -30) * mm, "endDerivative": vector(250, 30) * mm});
            skSolve(sketch);
        }
        {
            var Q0;
            Q0=qCreatedBy(makeId("Right.planeOp"),FACE);
            cPlane(context, id + "F73", {"entities" : qUnion([Q0]), "cplaneType" : CPlaneType.OFFSET, "offset" : 2000 * mm, "width" : 150 * mm, "height" : 150 * mm});
        }
        {
            var Q0;
            Q0=qCreatedBy(id+"F73.planeOp",FACE);
            var sketch = newSketch(context, id + "F74", { "sketchPlane" : qUnion([Q0])});
            skFitSpline(sketch, "E140", {"points": [v(7052.31, 2000) * mm, v(7177.31, 2010) * mm, v(7302.31, 2000) * mm], "startDerivative": vector(250, 30) * mm, "endDerivative": vector(250, -30) * mm});
            skFitSpline(sketch, "E141", {"points": [v(7052.31, 2000) * mm, v(7177.31, 1990) * mm, v(7302.31, 2000) * mm], "startDerivative": vector(250, -30) * mm, "endDerivative": vector(250, 30) * mm});
            skSolve(sketch);
        }
        {
            var Q1;
            Q1=qSketchRegion(id+"F70",true);
            var Q2;
            Q2=makeQuery(id+"F72.imprint","IMPRINT",FACE,{"disambiguationData":[TD([[makeQuery(id+"F72.imprint","IMPRINT",EDGE,{"derivedFrom":sQuery(id+"F72.wireOp",EDGE,"E138")}),-1.0]])]});
            var Q3;
            Q3=sQuery(id+"F69.wireOp",EDGE,"E132");
            var Q4;
            Q4=sQuery(id+"F69.wireOp",EDGE,"E134");
            loft(context, id + "F75", {"addGuides" : true, "sheetProfilesArray" : [{ "sheetProfileEntities" : qUnion([Q1]) }, { "sheetProfileEntities" : qUnion([Q2]) }], "guidesArray" : [{ "guideEntities" : qUnion([Q3]), "guideDerivativeType" : LoftGuideDerivativeType.DEFAULT, "guideDerivativeMagnitude" : 1 }, { "guideEntities" : qUnion([Q4]), "guideDerivativeType" : LoftGuideDerivativeType.DEFAULT, "guideDerivativeMagnitude" : 1 }]});
        }
        {
            var Q1;
            Q1=qSketchRegion(id+"F70",true);
            var Q2;
            Q2=makeQuery(id+"F74.imprint","IMPRINT",FACE,{"disambiguationData":[TD([[makeQuery(id+"F74.imprint","IMPRINT",EDGE,{"derivedFrom":sQuery(id+"F74.wireOp",EDGE,"E140")}),-1.0]])]});
            var Q3;
            Q3=sQuery(id+"F69.wireOp",EDGE,"E133");
            var Q4;
            Q4=sQuery(id+"F69.wireOp",EDGE,"E135");
            loft(context, id + "F76", {"operationType" : NewBodyOperationType.ADD, "addGuides" : true, "sheetProfilesArray" : [{ "sheetProfileEntities" : qUnion([Q1]) }, { "sheetProfileEntities" : qUnion([Q2]) }], "guidesArray" : [{ "guideEntities" : qUnion([Q3]), "guideDerivativeType" : LoftGuideDerivativeType.DEFAULT, "guideDerivativeMagnitude" : 1 }, { "guideEntities" : qUnion([Q4]), "guideDerivativeType" : LoftGuideDerivativeType.DEFAULT, "guideDerivativeMagnitude" : 1 }]});
        }
    });
